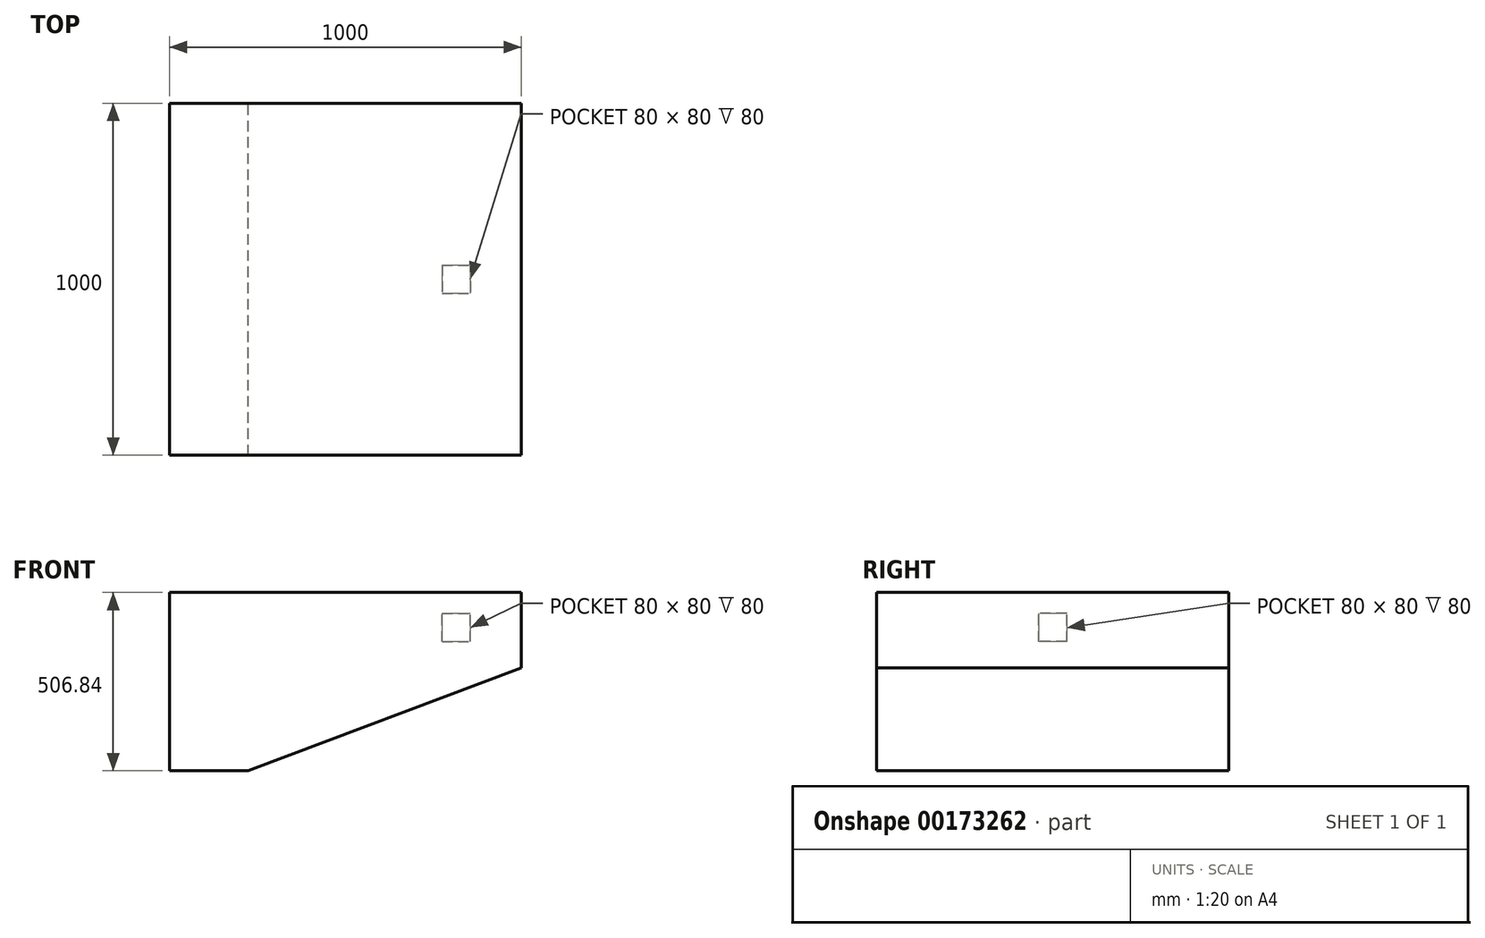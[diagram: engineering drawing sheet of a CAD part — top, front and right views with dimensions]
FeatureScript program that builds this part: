
annotation { "Feature Type Name" : "Feature", "Feature Type Description" : "" }
export const myFeature = defineFeature(function(context is Context, id is Id, definition is map)
    precondition{}
    {
        {
            var Q0;
            Q0=qCreatedBy(makeId("Front.planeOp"),FACE);
            var sketch = newSketch(context, id + "F0", { "sketchPlane" : qUnion([Q0])});
            skLineSegment(sketch, "E0", {"start": v(-529.64, -238.2) * mm, "end": v(-429.03, -238.2) * mm});
            skLineSegment(sketch, "E1", {"start": v(-429.03, -238.2) * mm, "end": v(348.05, 54.15) * mm});
            skLineSegment(sketch, "E2", {"start": v(348.05, 54.15) * mm, "end": v(348.05, 268.64) * mm});
            skLineSegment(sketch, "E3", {"start": v(348.05, 268.64) * mm, "end": v(-651.95, 268.64) * mm});
            skLineSegment(sketch, "E4", {"start": v(-651.95, 268.64) * mm, "end": v(-651.95, -238.2) * mm});
            skLineSegment(sketch, "E5", {"start": v(-651.95, -238.2) * mm, "end": v(-529.64, -238.2) * mm});
            skSolve(sketch);
        }
        {
            var Q0;
            Q0 = qSketchRegion(id + "F0", true);
            extrude(context, id + "F1", {"entities" : qUnion([Q0]), "endBound" : BoundingType.SYMMETRIC, "depth" : 1000 * mm});
        }
        {
            var Q0;
            Q0=qCreatedBy(makeId("Front.planeOp"),FACE);
            var sketch = newSketch(context, id + "F2", { "sketchPlane" : qUnion([Q0])});
            skLineSegment(sketch, "E6.bottom", {"start": v(122.26, 128.87) * mm, "end": v(202.26, 128.87) * mm});
            skLineSegment(sketch, "E6.top", {"start": v(122.26, 208.87) * mm, "end": v(202.26, 208.87) * mm});
            skLineSegment(sketch, "E6.left", {"start": v(122.26, 128.87) * mm, "end": v(122.26, 208.87) * mm});
            skLineSegment(sketch, "E6.right", {"start": v(202.26, 128.87) * mm, "end": v(202.26, 208.87) * mm});
            skSolve(sketch);
        }
        {
            var Q0;
            Q0 = qSketchRegion(id + "F2", true);
            extrude(context, id + "F3", {"entities" : qUnion([Q0]), "operationType" : NewBodyOperationType.REMOVE, "endBound" : BoundingType.SYMMETRIC, "oppositeDirection" : true, "depth" : 80 * mm});
        }
    });
